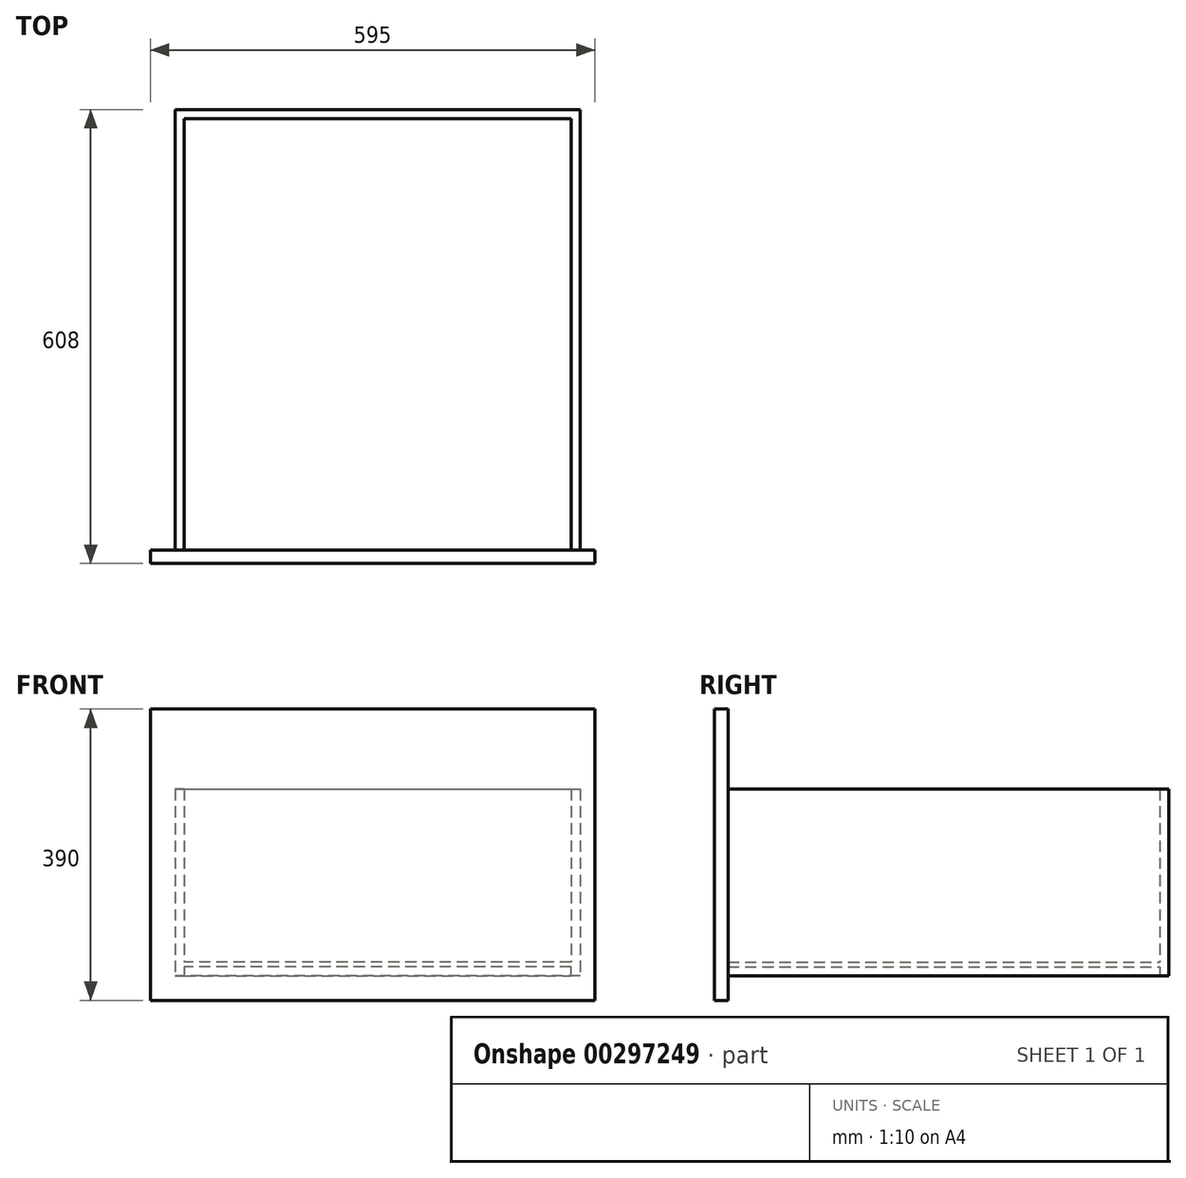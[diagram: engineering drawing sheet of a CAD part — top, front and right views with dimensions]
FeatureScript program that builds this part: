
annotation { "Feature Type Name" : "Feature", "Feature Type Description" : "" }
export const myFeature = defineFeature(function(context is Context, id is Id, definition is map)
    precondition{}
    {
        {
            var Q0;
            Q0=qCreatedBy(makeId("Front.planeOp"),FACE);
            var sketch = newSketch(context, id + "F0", { "sketchPlane" : qUnion([Q0])});
            skLineSegment(sketch, "E0.bottom", {"start": v(259, -3) * mm, "end": v(-259, -3) * mm});
            skLineSegment(sketch, "E0.top", {"start": v(259, 3) * mm, "end": v(-259, 3) * mm});
            skPoint(sketch, "E0.middle", {"position": v(0, 0) * mm});
            skLineSegment(sketch, "E1", {"start": v(-259, 3) * mm, "end": v(-259, 235) * mm});
            skLineSegment(sketch, "E2", {"start": v(-259, 235) * mm, "end": v(-271, 235) * mm});
            skLineSegment(sketch, "E3", {"start": v(-271, 235) * mm, "end": v(-271, -15) * mm});
            skLineSegment(sketch, "E4", {"start": v(-271, -15) * mm, "end": v(-259, -15) * mm});
            skLineSegment(sketch, "E5", {"start": v(-259, -15) * mm, "end": v(-259, -3) * mm});
            skLineSegment(sketch, "E6", {"start": v(259, 3) * mm, "end": v(259, 235) * mm});
            skLineSegment(sketch, "E7", {"start": v(259, 235) * mm, "end": v(271, 235) * mm});
            skLineSegment(sketch, "E8", {"start": v(271, 235) * mm, "end": v(271, -15) * mm});
            skLineSegment(sketch, "E9", {"start": v(271, -15) * mm, "end": v(259, -15) * mm});
            skLineSegment(sketch, "E10", {"start": v(259, -15) * mm, "end": v(259, -3) * mm});
            skSolve(sketch);
        }
        {
            var Q0;
            Q0 = qSketchRegion(id + "F0", true);
            extrude(context, id + "F1", {"entities" : qUnion([Q0]), "depth" : 590 * mm});
        }
        {
            var Q0;
            Q0=makeQuery(id+"F1.opExtrude","SWEPT_FACE",FACE,{"disambiguationData":[OSD([sQuery(id+"F0.wireOp",EDGE,"E6")])]});
            var sketch = newSketch(context, id + "F2", { "sketchPlane" : qUnion([Q0])});
            skLineSegment(sketch, "E11.bottom", {"start": v(0, 235) * mm, "end": v(12, 235) * mm});
            skLineSegment(sketch, "E11.top", {"start": v(0, -15) * mm, "end": v(12, -15) * mm});
            skLineSegment(sketch, "E11.left", {"start": v(0, 235) * mm, "end": v(0, -15) * mm});
            skLineSegment(sketch, "E11.right", {"start": v(12, 235) * mm, "end": v(12, -15) * mm});
            skSolve(sketch);
        }
        {
            var Q0;
            Q0 = qSketchRegion(id + "F2", true);
            extrude(context, id + "F3", {"entities" : qUnion([Q0]), "operationType" : NewBodyOperationType.ADD, "depth" : 518 * mm});
        }
        {
            var Q0;
            Q0=makeQuery(id+"F1.opExtrude","CAP_FACE",FACE,{"disambiguationData":[OSD([sQuery(id+"F0.wireOp",EDGE,"E0.bottom"),sQuery(id+"F0.wireOp",EDGE,"E0.top"),sQuery(id+"F0.wireOp",EDGE,"E1"),sQuery(id+"F0.wireOp",EDGE,"E2"),sQuery(id+"F0.wireOp",EDGE,"E3"),sQuery(id+"F0.wireOp",EDGE,"E4"),sQuery(id+"F0.wireOp",EDGE,"E5"),sQuery(id+"F0.wireOp",EDGE,"E6"),sQuery(id+"F0.wireOp",EDGE,"E7"),sQuery(id+"F0.wireOp",EDGE,"E8"),sQuery(id+"F0.wireOp",EDGE,"E9"),sQuery(id+"F0.wireOp",EDGE,"E10")])],"isStart":false});
            var sketch = newSketch(context, id + "F4", { "sketchPlane" : qUnion([Q0])});
            skLineSegment(sketch, "E12.bottom", {"start": v(-304, 342) * mm, "end": v(291, 342) * mm});
            skLineSegment(sketch, "E12.top", {"start": v(-304, -48) * mm, "end": v(291, -48) * mm});
            skLineSegment(sketch, "E12.left", {"start": v(-304, 342) * mm, "end": v(-304, -48) * mm});
            skLineSegment(sketch, "E12.right", {"start": v(291, 342) * mm, "end": v(291, -48) * mm});
            skSolve(sketch);
        }
        {
            var Q0;
            Q0 = qSketchRegion(id + "F4", true);
            extrude(context, id + "F5", {"entities" : qUnion([Q0]), "operationType" : NewBodyOperationType.ADD, "depth" : 18 * mm});
        }
    });
